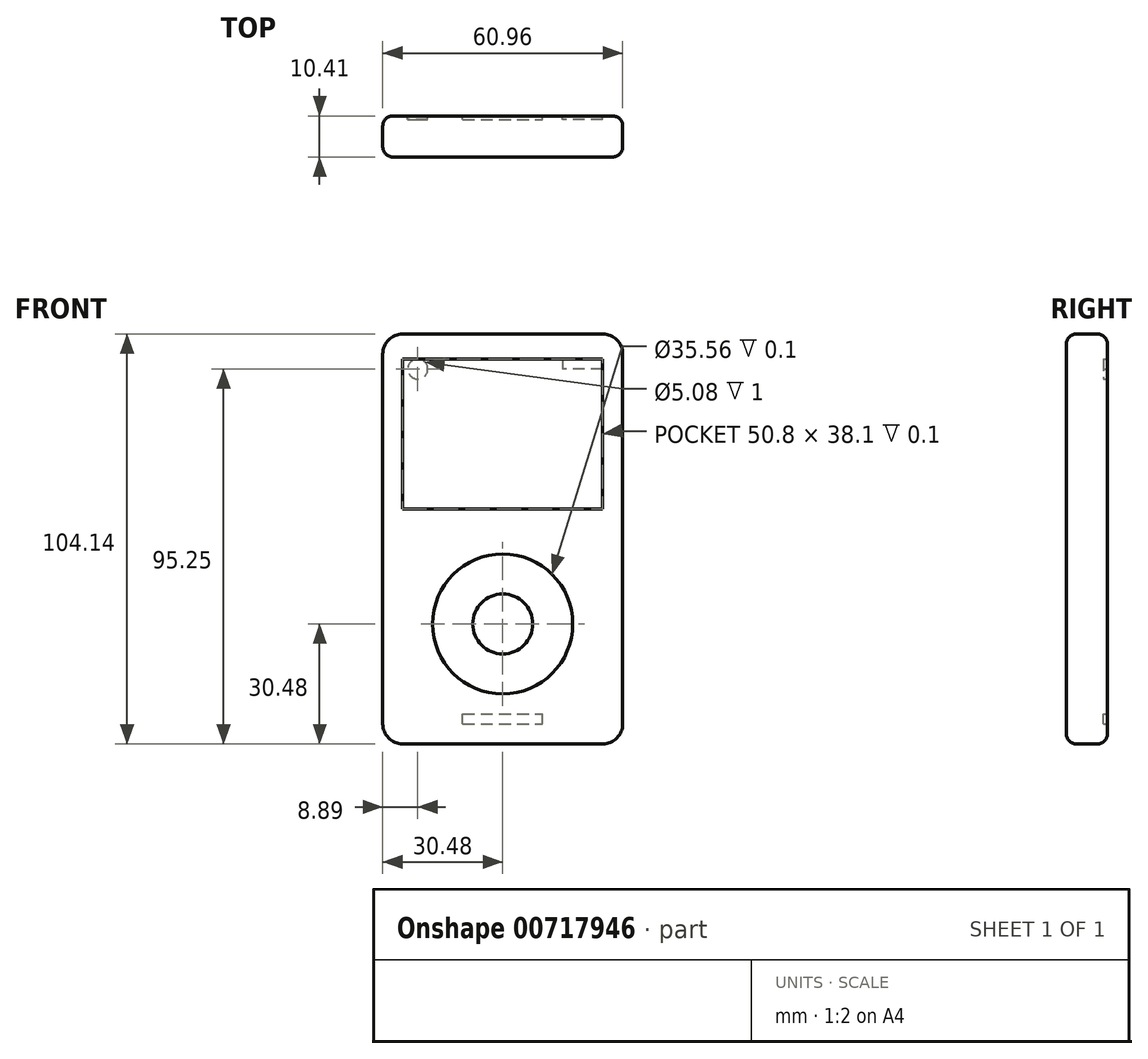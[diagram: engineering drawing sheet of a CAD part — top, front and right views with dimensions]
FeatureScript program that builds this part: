
annotation { "Feature Type Name" : "Feature", "Feature Type Description" : "" }
export const myFeature = defineFeature(function(context is Context, id is Id, definition is map)
    precondition{}
    {
        {
            var Q0;
            Q0=qCreatedBy(makeId("Front.planeOp"),FACE);
            var sketch = newSketch(context, id + "F0", { "sketchPlane" : qUnion([Q0])});
            skLineSegment(sketch, "E0.bottom", {"start": v(25.4, 52.07) * mm, "end": v(-25.4, 52.07) * mm});
            skLineSegment(sketch, "E0.top", {"start": v(25.4, -52.07) * mm, "end": v(-25.4, -52.07) * mm});
            skLineSegment(sketch, "E0.left", {"start": v(30.48, 47) * mm, "end": v(30.48, -46.99) * mm});
            skLineSegment(sketch, "E0.right", {"start": v(-30.48, 47) * mm, "end": v(-30.48, -46.99) * mm});
            skPoint(sketch, "E0.middle", {"position": v(0, 0) * mm});
            skPoint(sketch, "E1.visualSharp", {"position": v(-30.48, 52.07) * mm});
            skArc(sketch, "E1.filletArc", {"start": v(-25.4, 52.07) * mm, "mid": v(-29, 50.58) * mm, "end": v(-30.48, 47) * mm});
            skPoint(sketch, "E2.visualSharp", {"position": v(30.48, 52.07) * mm});
            skArc(sketch, "E2.filletArc", {"start": v(30.48, 47) * mm, "mid": v(29, 50.58) * mm, "end": v(25.4, 52.07) * mm});
            skPoint(sketch, "E3.visualSharp", {"position": v(30.48, -52.07) * mm});
            skArc(sketch, "E3.filletArc", {"start": v(25.4, -52.07) * mm, "mid": v(29, -50.58) * mm, "end": v(30.48, -46.99) * mm});
            skPoint(sketch, "E4.visualSharp", {"position": v(-30.48, -52.07) * mm});
            skArc(sketch, "E4.filletArc", {"start": v(-30.48, -46.99) * mm, "mid": v(-29, -50.58) * mm, "end": v(-25.4, -52.07) * mm});
            skLineSegment(sketch, "E5.bottom", {"start": v(25.4, 7.62) * mm, "end": v(-25.4, 7.62) * mm});
            skLineSegment(sketch, "E5.top", {"start": v(25.4, 45.72) * mm, "end": v(-25.4, 45.72) * mm});
            skLineSegment(sketch, "E5.left", {"start": v(25.4, 7.62) * mm, "end": v(25.4, 45.72) * mm});
            skLineSegment(sketch, "E5.right", {"start": v(-25.4, 7.62) * mm, "end": v(-25.4, 45.72) * mm});
            skPoint(sketch, "E5.middle", {"position": v(0, 26.67) * mm});
            skCircle(sketch, "E6", {"center": v(0, -21.59) * mm, "radius": 7.62 * mm});
            skCircle(sketch, "E7", {"center": v(0, -21.59) * mm, "radius": 17.78 * mm});
            skSolve(sketch);
        }
        {
            var Q0;
            Q0=makeQuery(id+"F0.imprint","IMPRINT",FACE,{"disambiguationData":[TD([[makeQuery(id+"F0.imprint","IMPRINT",EDGE,{"derivedFrom":sQuery(id+"F0.wireOp",EDGE,"E6")}),1.0]])]});
            var Q1;
            Q1=makeQuery(id+"F0.imprint","IMPRINT",FACE,{"disambiguationData":[TD([[makeQuery(id+"F0.imprint","IMPRINT",EDGE,{"derivedFrom":sQuery(id+"F0.wireOp",EDGE,"E6")}),-1.0]])]});
            var Q2;
            Q2=makeQuery(id+"F0.imprint","IMPRINT",FACE,{"disambiguationData":[TD([[makeQuery(id+"F0.imprint","IMPRINT",EDGE,{"derivedFrom":sQuery(id+"F0.wireOp",EDGE,"E5.bottom")}),-1.0]])]});
            var Q3;
            Q3=makeQuery(id+"F0.imprint","IMPRINT",FACE,{"disambiguationData":[TD([[makeQuery(id+"F0.imprint","IMPRINT",EDGE,{"derivedFrom":sQuery(id+"F0.wireOp",EDGE,"E0.bottom")}),1.0]])]});
            extrude(context, id + "F1", {"entities" : qUnion([Q0, Q1, Q2, Q3]), "oppositeDirection" : true, "depth" : 10.4 * mm, "offsetDistance" : 25.4 * mm});
        }
        {
            var Q0;
            Q0=makeQuery(id+"F0.imprint","IMPRINT",FACE,{"disambiguationData":[TD([[makeQuery(id+"F0.imprint","IMPRINT",EDGE,{"derivedFrom":sQuery(id+"F0.wireOp",EDGE,"E5.bottom")}),-1.0]])]});
            var Q1;
            Q1=makeQuery(id+"F0.imprint","IMPRINT",FACE,{"disambiguationData":[TD([[makeQuery(id+"F0.imprint","IMPRINT",EDGE,{"derivedFrom":sQuery(id+"F0.wireOp",EDGE,"E6")}),-1.0]])]});
            extrude(context, id + "F2", {"entities" : qUnion([Q0, Q1]), "operationType" : NewBodyOperationType.REMOVE, "oppositeDirection" : true, "depth" : .1 * mm, "offsetDistance" : 25.4 * mm});
        }
        {
            var Q0;
            Q0=makeQuery(id+"F1.opExtrude","CAP_FACE",FACE,{"disambiguationData":[OSD([sQuery(id+"F0.wireOp",EDGE,"E0.bottom"),sQuery(id+"F0.wireOp",EDGE,"E0.top"),sQuery(id+"F0.wireOp",EDGE,"E0.left"),sQuery(id+"F0.wireOp",EDGE,"E0.right"),sQuery(id+"F0.wireOp",EDGE,"E1.filletArc"),sQuery(id+"F0.wireOp",EDGE,"E2.filletArc"),sQuery(id+"F0.wireOp",EDGE,"E3.filletArc"),sQuery(id+"F0.wireOp",EDGE,"E4.filletArc")])],"isStart":false});
            var sketch = newSketch(context, id + "F3", { "sketchPlane" : qUnion([Q0])});
            skLineSegment(sketch, "E8.bottom", {"start": v(10.16, -46.99) * mm, "end": v(-10.16, -46.99) * mm});
            skLineSegment(sketch, "E8.top", {"start": v(10.16, -44.45) * mm, "end": v(-10.16, -44.45) * mm});
            skLineSegment(sketch, "E8.left", {"start": v(10.16, -46.99) * mm, "end": v(10.16, -44.45) * mm});
            skLineSegment(sketch, "E8.right", {"start": v(-10.16, -46.99) * mm, "end": v(-10.16, -44.45) * mm});
            skPoint(sketch, "E8.middle", {"position": v(0, -45.72) * mm});
            skLineSegment(sketch, "E9.bottom", {"start": v(-25.4, 45.72) * mm, "end": v(-15.24, 45.72) * mm});
            skLineSegment(sketch, "E9.top", {"start": v(-25.4, 43.18) * mm, "end": v(-15.24, 43.18) * mm});
            skLineSegment(sketch, "E9.left", {"start": v(-25.4, 45.72) * mm, "end": v(-25.4, 43.18) * mm});
            skLineSegment(sketch, "E9.right", {"start": v(-15.24, 45.72) * mm, "end": v(-15.24, 43.18) * mm});
            skCircle(sketch, "E10", {"center": v(21.59, 43.18) * mm, "radius": 2.54 * mm});
            skSolve(sketch);
        }
        {
            var Q0;
            Q0=makeQuery(id+"F3.imprint","IMPRINT",FACE,{"disambiguationData":[TD([[makeQuery(id+"F3.imprint","IMPRINT",EDGE,{"derivedFrom":sQuery(id+"F3.wireOp",EDGE,"E9.bottom")}),-1.0]])]});
            var Q1;
            Q1=makeQuery(id+"F3.imprint","IMPRINT",FACE,{"disambiguationData":[TD([[makeQuery(id+"F3.imprint","IMPRINT",EDGE,{"derivedFrom":sQuery(id+"F3.wireOp",EDGE,"E10")}),1.0]])]});
            var Q2;
            Q2=makeQuery(id+"F3.imprint","IMPRINT",FACE,{"disambiguationData":[TD([[makeQuery(id+"F3.imprint","IMPRINT",EDGE,{"derivedFrom":sQuery(id+"F3.wireOp",EDGE,"E8.bottom")}),-1.0]])]});
            extrude(context, id + "F4", {"entities" : qUnion([Q0, Q1, Q2]), "operationType" : NewBodyOperationType.REMOVE, "oppositeDirection" : true, "depth" : 1 * mm, "offsetDistance" : 25.4 * mm});
        }
        {
            var Q0;
            Q0=makeQuery(id+"F1.opExtrude","CAP_EDGE",EDGE,{"disambiguationData":[OSD([sQuery(id+"F0.wireOp",EDGE,"E0.left")])],"isStart":true});
            var Q1;
            Q1=makeQuery(id+"F1.opExtrude","CAP_EDGE",EDGE,{"disambiguationData":[OSD([sQuery(id+"F0.wireOp",EDGE,"E0.left")])],"isStart":false});
            fillet(context, id + "F5", {"entities" : qUnion([Q0, Q1]), "radius" : 2.54 * mm, "tangentPropagation" : true, "allowEdgeOverflow" : false});
        }
    });
